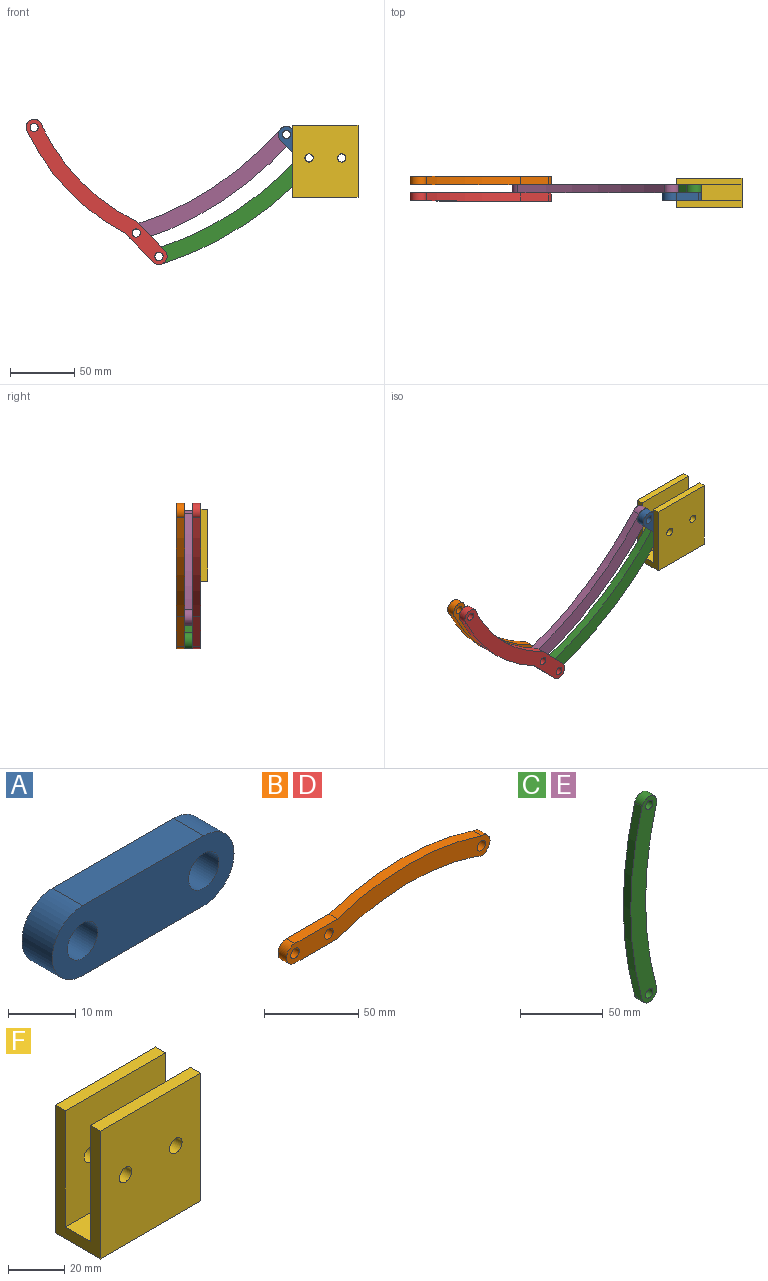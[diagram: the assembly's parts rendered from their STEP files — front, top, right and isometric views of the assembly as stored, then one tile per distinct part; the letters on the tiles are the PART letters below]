
ASSEMBLY  parts=6 mates=7
PART A: 8 faces, bbox 38.1x6.4x12.7 mm
  f0: cylinder r=6.35mm len=12.7mm, axis (0,1,0), area 126.7mm2, adj f1,f3,f6,f7
  f1: plane 25.4x6.35mm, normal (0,0,-1), area 161.3mm2, adj f0,f2,f6,f7
  f2: cylinder r=6.35mm len=12.7mm, axis (0,1,0), area 126.7mm2, adj f1,f3,f6,f7
  f3: plane 25.4x6.35mm, normal (0,0,1), area 161.3mm2, adj f0,f2,f6,f7
  f4: cylinder r=3.17mm len=6.35mm, axis (0,1,0), area 126.7mm2, adj f6,f7
  f5: cylinder r=3.17mm len=6.35mm, axis (0,1,0), area 126.7mm2, adj f6,f7
  f6: plane 38.1x12.7mm, normal (0,-1,0), area 385.9mm2, adj f0,f1,f2,f3,f4,f5
  f7: plane 38.1x12.7mm, normal (0,1,0), area 385.9mm2, adj f0,f1,f2,f3,f4,f5
PART B: 11 faces, bbox 152.4x6.4x21.5 mm
  f0: cylinder r=6.35mm len=12.7mm, axis (0,1,0), area 153.8mm2, adj f1,f7,f9,f10
  f1: cylinder r=169.68mm len=107.95mm, axis (0,1,0), area 697.6mm2, adj f0,f2,f9,f10
  f2: plane 31.75x6.35mm, normal (0,0,1), area 201.6mm2, adj f1,f3,f9,f10
  f3: cylinder r=6.35mm len=12.7mm, axis (0,1,0), area 126.7mm2, adj f2,f4,f9,f10
  f4: plane 31.75x6.35mm, normal (0,0,-1), area 201.6mm2, adj f3,f7,f9,f10
  f5: cylinder r=3.17mm len=6.35mm, axis (0,1,0), area 126.7mm2, adj f9,f10
  f6: cylinder r=3.17mm len=6.35mm, axis (0,1,0), area 126.7mm2, adj f9,f10
  f7: cylinder r=157.69mm len=104mm, axis (0,1,0), area 673mm2, adj f0,f4,f9,f10
  f8: cylinder r=3.17mm len=6.35mm, axis (0,1,0), area 126.7mm2, adj f9,f10
  f9: plane 152.4x21.51mm, normal (0,-1,0), area 1754.8mm2, adj f0,f1,f2,f3,f4,f5,f6,f7
  f10: plane 152.4x21.51mm, normal (0,1,0), area 1754.8mm2, adj f0,f1,f2,f3,f4,f5,f6,f7
PART C: 8 faces, bbox 22.2x6.4x152.4 mm
  f0: cylinder r=254.53mm len=136.3mm, axis (0,1,0), area 876.2mm2, adj f1,f3,f6,f7
  f1: cylinder r=6.35mm len=12.47mm, axis (0,1,0), area 126.7mm2, adj f0,f2,f6,f7
  f2: cylinder r=267.23mm len=143.1mm, axis (0,1,0), area 919.9mm2, adj f1,f3,f6,f7
  f3: cylinder r=6.35mm len=12.47mm, axis (0,1,0), area 126.7mm2, adj f0,f2,f6,f7
  f4: cylinder r=3.17mm len=6.35mm, axis (0,1,0), area 126.7mm2, adj f6,f7
  f5: cylinder r=3.17mm len=6.35mm, axis (0,1,0), area 126.7mm2, adj f6,f7
  f6: plane 152.4x22.23mm, normal (0,-1,0), area 1859.4mm2, adj f0,f1,f2,f3,f4,f5
  f7: plane 152.4x22.23mm, normal (0,1,0), area 1859.4mm2, adj f0,f1,f2,f3,f4,f5
PART D: same geometry as B
PART E: same geometry as C
PART F: 14 faces, bbox 50.8x22.9x55.9 mm
  f0: plane 55.88x50.8mm, normal (0,-1,0), area 2775.4mm2, adj f5,f6,f8,f9,f10,f11
  f1: plane 55.88x50.8mm, normal (0,1,0), area 2775.4mm2, adj f6,f7,f8,f9,f12,f13
  f2: plane 50.8x50.8mm, normal (0,-1,0), area 2517.3mm2, adj f4,f7,f8,f9,f12,f13
  f3: plane 50.8x50.8mm, normal (0,1,0), area 2517.3mm2, adj f4,f5,f8,f9,f10,f11
  f4: plane 50.8x12.7mm, normal (0,0,1), area 645.2mm2, adj f2,f3,f8,f9
  f5: plane 50.8x5.08mm, normal (0,0,1), area 258.1mm2, adj f0,f3,f8,f9
  f6: plane 50.8x22.86mm, normal (0,0,-1), area 1161.3mm2, adj f0,f1,f8,f9
  f7: plane 50.8x5.08mm, normal (0,0,1), area 258.1mm2, adj f1,f2,f8,f9
  f8: plane 55.88x22.86mm, normal (1,0,0), area 632.3mm2, adj f0,f1,f2,f3,f4,f5,f6,f7
  f9: plane 55.88x22.86mm, normal (-1,0,0), area 632.3mm2, adj f0,f1,f2,f3,f4,f5,f6,f7
  f10: cylinder r=3.17mm len=6.35mm, axis (0,-1,0), area 101.3mm2, adj f0,f3
  f11: cylinder r=3.17mm len=6.35mm, axis (0,-1,0), area 101.3mm2, adj f0,f3
  f12: cylinder r=3.17mm len=6.35mm, axis (0,-1,0), area 101.3mm2, adj f1,f2
  f13: cylinder r=3.17mm len=6.35mm, axis (0,-1,0), area 101.3mm2, adj f1,f2
PLACE A rot(axis=(0,-1,0),134.1deg) t=(-59.67,50.13,22.81)mm
PLACE B rot(axis=(0,-1,0),134.1deg) t=(-176.45,62.83,-53.86)mm
PLACE C rot(axis=(0,-1,0),123.3deg) t=(-58.55,56.48,17.59)mm
PLACE D rot(axis=(0,-1,0),134.1deg) t=(-176.45,50.13,-53.86)mm
PLACE E rot(axis=(0,-1,0),123.3deg) t=(-76.22,56.48,35.84)mm
PLACE F t=(-99.45,38.7,-11.13)mm fixed
MATE revolute D.f3 <-> C.f1  axis (0,1,0) through (-203.54,38.7,-62.4)mm
MATE revolute E.f3 <-> A.f2  axis (0,-1,0) through (-104.42,38.7,32.52)mm
MATE revolute A.f0 <-> C.f3  axis (0,1,0) through (-86.75,38.7,14.27)mm
MATE cylindrical E.f1 <-> D.f8  axis (0,1,0) through (-221.2,45.05,-44.15)mm
MATE cylindrical B.f8 <-> E.f1  axis (0,-1,0) through (-221.2,45.05,-44.15)mm
MATE revolute F.f11 <-> C.f3  axis (0,-1,0) through (-86.75,45.05,14.27)mm
MATE revolute C.f1 <-> B.f3  axis (0,1,0) through (-203.54,45.05,-62.4)mm
